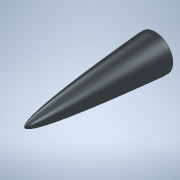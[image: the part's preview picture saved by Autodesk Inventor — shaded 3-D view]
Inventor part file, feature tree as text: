
AUTODESK INVENTOR PART (.ipt)
format: ipt  version: 2020 (Build 240168000, 168)  size: 210,944 bytes
history: native  units: mm
features: revolve x1, sketch x1
ambient origin geometry x8: Origin, YZ Plane, XZ Plane, XY Plane, X Axis, Y Axis, Z Axis, Center Point
bodies: Body1 (feature_tree)
feature tree (2):
  revolve  "Revolution4"  Angle=90.0deg
  sketch  "Sketch1"  dims[d44=10.0mm d60=90.0deg d62=15.0mm d63=1.8mm d64=118.2mm d65=120.0mm d11=0.872665mm d12=0.872665mm]
